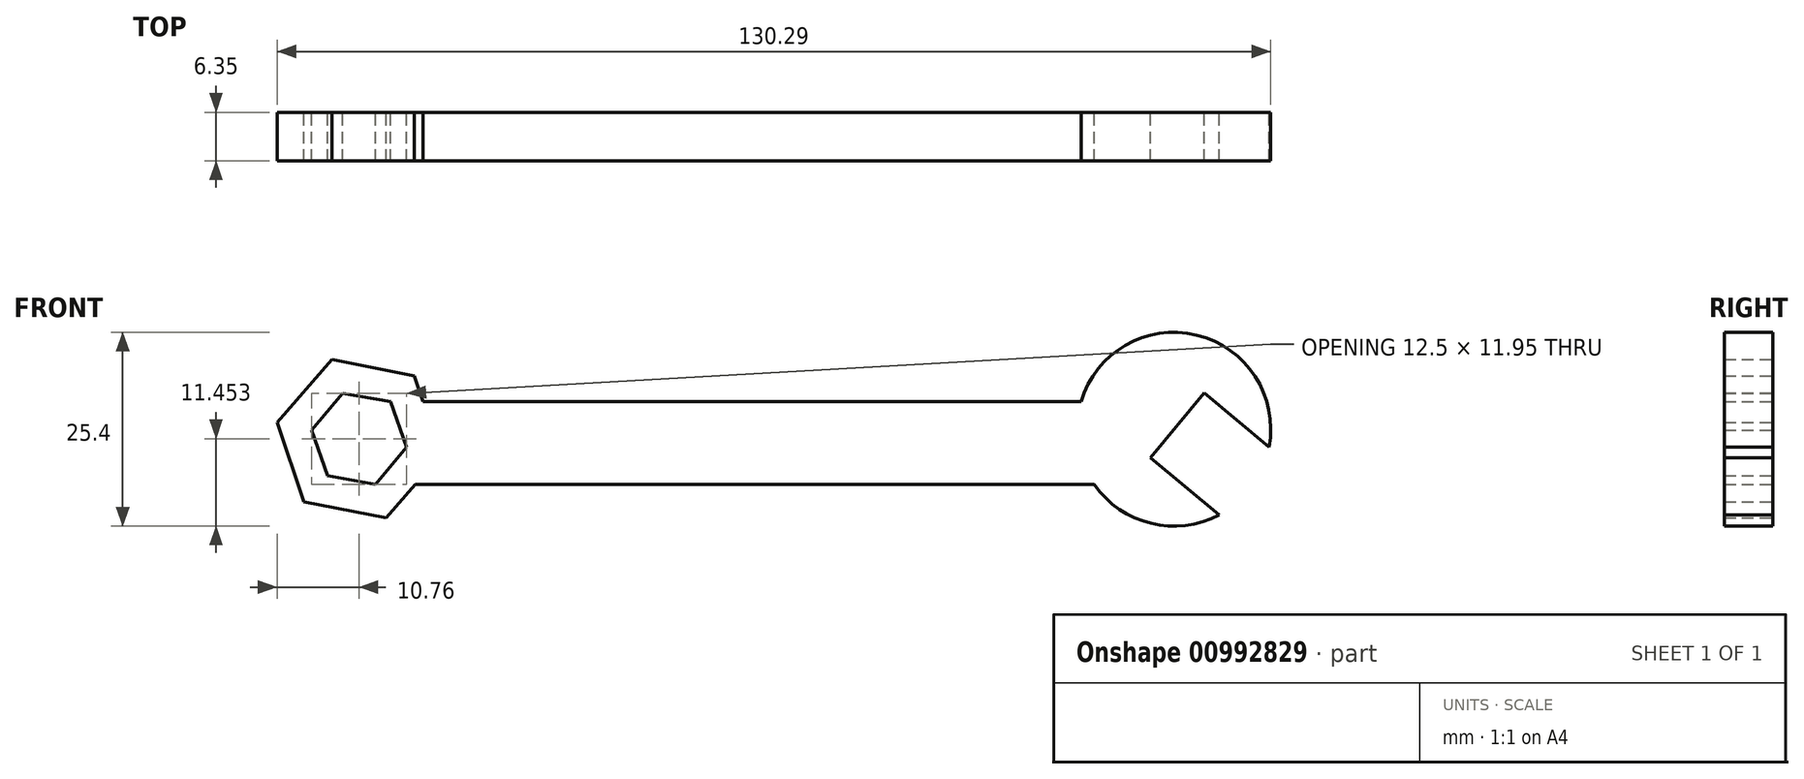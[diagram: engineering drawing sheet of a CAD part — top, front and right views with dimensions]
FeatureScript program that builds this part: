
annotation { "Feature Type Name" : "Feature", "Feature Type Description" : "" }
export const myFeature = defineFeature(function(context is Context, id is Id, definition is map)
    precondition{}
    {
        {
            var Q0;
            Q0=qCreatedBy(makeId("Front.planeOp"),FACE);
            var sketch = newSketch(context, id + "F0", { "sketchPlane" : qUnion([Q0])});
            skCircle(sketch, "E0", {"center": v(80.09, 47.85) * mm, "radius": 12.7 * mm});
            skCircle(sketch, "E1.cCircle", {"center": v(-26.74, 46.6) * mm, "radius": 5.5 * mm, "construction": true});
            skLineSegment(sketch, "E1.0", {"start": v(-32.99, 47.73) * mm, "end": v(-28.89, 52.58) * mm});
            skLineSegment(sketch, "E1.1", {"start": v(-28.89, 52.58) * mm, "end": v(-22.64, 51.45) * mm});
            skLineSegment(sketch, "E1.2", {"start": v(-22.64, 51.45) * mm, "end": v(-20.5, 45.47) * mm});
            skLineSegment(sketch, "E1.3", {"start": v(-20.5, 45.47) * mm, "end": v(-24.6, 40.63) * mm});
            skLineSegment(sketch, "E1.4", {"start": v(-24.6, 40.63) * mm, "end": v(-30.84, 41.76) * mm});
            skLineSegment(sketch, "E1.5", {"start": v(-30.84, 41.76) * mm, "end": v(-32.99, 47.73) * mm});
            skPoint(sketch, "E1.0.midPoint", {"position": v(-30.94, 50.16) * mm});
            skLineSegment(sketch, "E2.bottom", {"start": v(-24.6, 40.63) * mm, "end": v(77, 40.63) * mm});
            skLineSegment(sketch, "E2.top", {"start": v(-24.6, 51.45) * mm, "end": v(77, 51.45) * mm});
            skLineSegment(sketch, "E2.left", {"start": v(-24.6, 40.63) * mm, "end": v(-24.6, 51.45) * mm});
            skLineSegment(sketch, "E2.right", {"start": v(77, 40.63) * mm, "end": v(77, 51.45) * mm});
            skLineSegment(sketch, "E3", {"start": v(92.57, 45.51) * mm, "end": v(84.03, 52.6) * mm});
            skLineSegment(sketch, "E4", {"start": v(84.03, 52.6) * mm, "end": v(77, 44.14) * mm});
            skPoint(sketch, "E4.endSnap0", {"position": v(77, 46.04) * mm});
            skLineSegment(sketch, "E5", {"start": v(77, 44.14) * mm, "end": v(86.05, 36.63) * mm});
            skCircle(sketch, "E6.cCircle", {"center": v(-26.74, 46.6) * mm, "radius": 9.5 * mm, "construction": true});
            skLineSegment(sketch, "E6.0", {"start": v(-37.5, 48.72) * mm, "end": v(-30.29, 56.98) * mm});
            skLineSegment(sketch, "E6.1", {"start": v(-30.29, 56.98) * mm, "end": v(-19.52, 54.87) * mm});
            skLineSegment(sketch, "E6.2", {"start": v(-19.52, 54.87) * mm, "end": v(-15.98, 44.48) * mm});
            skLineSegment(sketch, "E6.3", {"start": v(-15.98, 44.48) * mm, "end": v(-23.2, 36.22) * mm});
            skLineSegment(sketch, "E6.4", {"start": v(-23.2, 36.22) * mm, "end": v(-33.96, 38.34) * mm});
            skLineSegment(sketch, "E6.5", {"start": v(-33.96, 38.34) * mm, "end": v(-37.5, 48.72) * mm});
            skPoint(sketch, "E6.0.midPoint", {"position": v(-33.9, 52.85) * mm});
            skSolve(sketch);
        }
        {
            var Q0;
            {var subQ5=sQuery(id+"F0.wireOp",EDGE,"E0");var subQ7=sQuery(id+"F0.wireOp",EDGE,"E2.bottom");var subQ8=makeQuery(id+"F0.imprint","INTERSECT",VERTEX,{"derivedFrom":[subQ5,subQ7]});Q0=makeQuery(id+"F0.imprint","IMPRINT",FACE,{"disambiguationData":[TD([[makeQuery(id+"F0.imprint","IMPRINT",EDGE,{"disambiguationData":[TD([[subQ8,1.0]])],"derivedFrom":subQ5}),-1.0]])]});}
            var Q1;
            {var subQ1=sQuery(id+"F0.wireOp",EDGE,"E2.bottom");var subQ6=sQuery(id+"F0.wireOp",EDGE,"E0");var subQ8=makeQuery(id+"F0.imprint","INTERSECT",VERTEX,{"derivedFrom":[subQ6,subQ1]});Q1=makeQuery(id+"F0.imprint","IMPRINT",FACE,{"disambiguationData":[TD([[makeQuery(id+"F0.imprint","IMPRINT",EDGE,{"disambiguationData":[TD([[subQ8,1.0]])],"derivedFrom":subQ6}),1.0]])]});}
            var Q2;
            {var subQ0=sQuery(id+"F0.wireOp",EDGE,"E3");Q2=makeQuery(id+"F0.imprint","IMPRINT",FACE,{"disambiguationData":[TD([[makeQuery(id+"F0.imprint","IMPRINT",EDGE,{"derivedFrom":subQ0}),-1.0]])]});}
            var Q3;
            {var subQ0=sQuery(id+"F0.wireOp",EDGE,"E5");Q3=makeQuery(id+"F0.imprint","IMPRINT",FACE,{"disambiguationData":[TD([[makeQuery(id+"F0.imprint","IMPRINT",EDGE,{"derivedFrom":subQ0}),-1.0]])]});}
            var Q4;
            {var subQ1=sQuery(id+"F0.wireOp",EDGE,"E1.2");Q4=makeQuery(id+"F0.imprint","IMPRINT",FACE,{"disambiguationData":[TD([[makeQuery(id+"F0.imprint","IMPRINT",EDGE,{"derivedFrom":subQ1}),1.0]])]});}
            var Q5;
            Q5=makeQuery(id+"F0.imprint","IMPRINT",FACE,{"disambiguationData":[TD([[makeQuery(id+"F0.imprint","IMPRINT",EDGE,{"derivedFrom":sQuery(id+"F0.wireOp",EDGE,"E1.0")}),1.0]])]});
            extrude(context, id + "F1", {"entities" : qUnion([Q0, Q1, Q2, Q3, Q4, Q5]), "depth" : 6.35 * mm, "offsetDistance" : 25.4 * mm});
        }
    });
